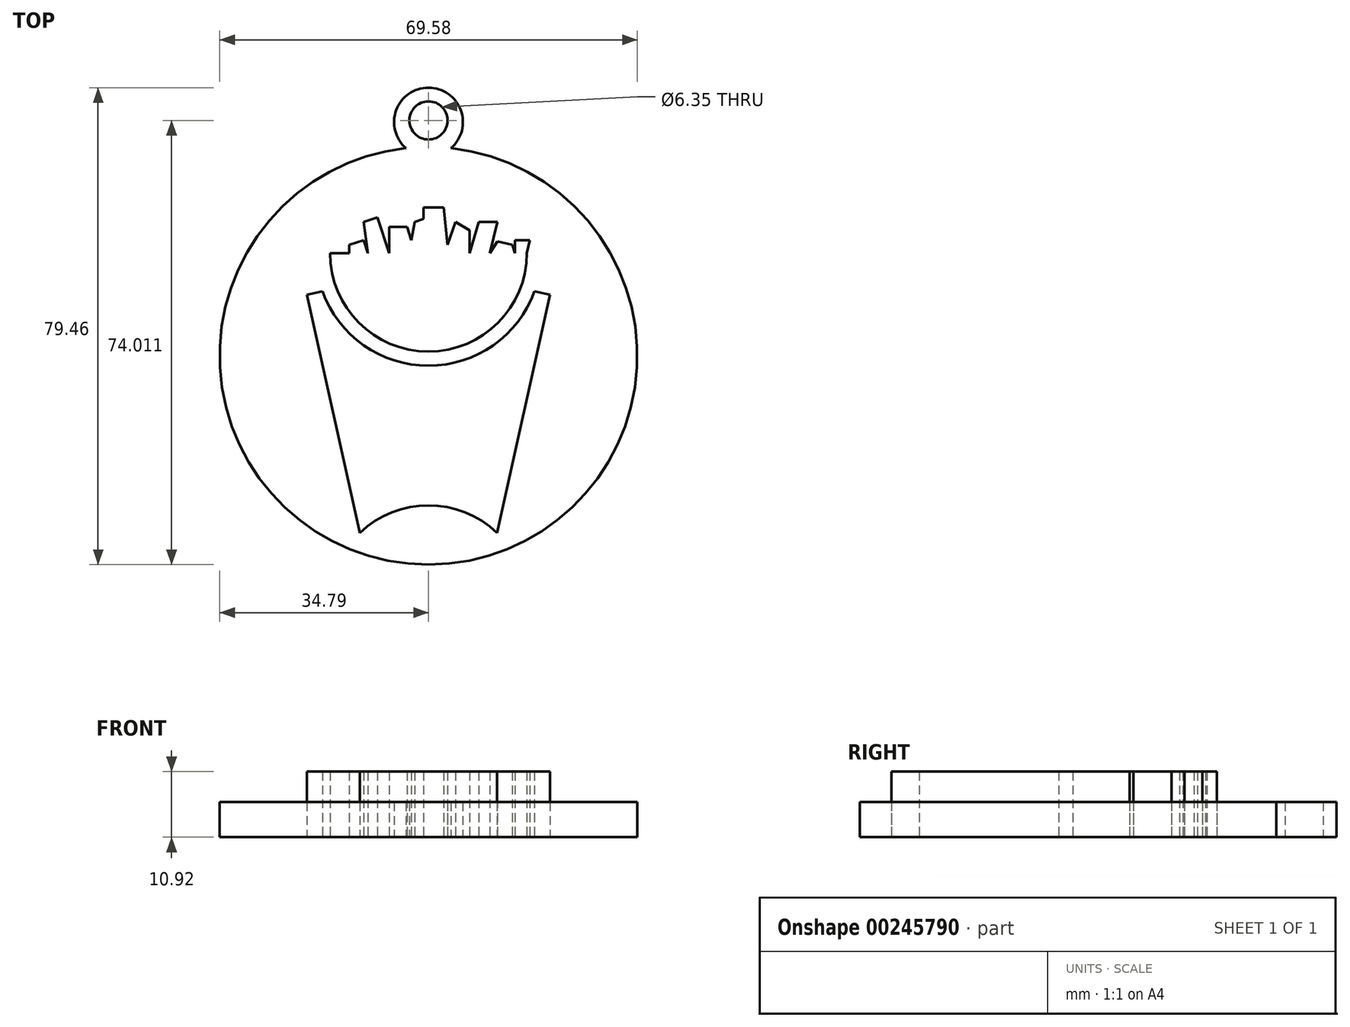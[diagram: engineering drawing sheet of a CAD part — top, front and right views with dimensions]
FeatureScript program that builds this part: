
annotation { "Feature Type Name" : "Feature", "Feature Type Description" : "" }
export const myFeature = defineFeature(function(context is Context, id is Id, definition is map)
    precondition{}
    {
        {
            var Q0;
            Q0=qCreatedBy(makeId("Top.planeOp"),FACE);
            var sketch = newSketch(context, id + "F0", { "sketchPlane" : qUnion([Q0])});
            skCircle(sketch, "E0", {"center": v(0, 0) * mm, "radius": 65.8 * mm});
            skCircle(sketch, "E1", {"center": v(0, 0) * mm, "radius": 57.75 * mm});
            skArc(sketch, "E2", {"start": v(0, 0.7) * mm, "mid": v(11.6, 5.51) * mm, "end": v(16.4, 17.11) * mm});
            skLineSegment(sketch, "E3", {"start": v(11.45, -29.5) * mm, "end": v(20.28, 10.19) * mm});
            skLineSegment(sketch, "E4", {"start": v(20.28, 10.19) * mm, "end": v(17.67, 10.77) * mm});
            skArc(sketch, "E5", {"start": v(0, -1.66) * mm, "mid": v(10.8, 1.76) * mm, "end": v(17.67, 10.77) * mm});
            skArc(sketch, "E6.trimOffspring", {"start": v(11.45, -29.5) * mm, "mid": v(6.17, -26.1) * mm, "end": v(0, -24.92) * mm});
            skLineSegment(sketch, "E7.MirrorCS", {"start": v(-13.24, 17.11) * mm, "end": v(-16.4, 17.11) * mm});
            skArc(sketch, "E8.MirrorCS", {"start": v(0, -1.66) * mm, "mid": v(-10.8, 1.76) * mm, "end": v(-17.67, 10.77) * mm});
            skLineSegment(sketch, "E9.MirrorCS", {"start": v(-11.45, -29.5) * mm, "end": v(-20.28, 10.19) * mm});
            skArc(sketch, "E10.MirrorCS", {"start": v(-11.45, -29.5) * mm, "mid": v(-6.17, -26.1) * mm, "end": v(0, -24.92) * mm});
            skLineSegment(sketch, "E11.MirrorCS", {"start": v(-20.28, 10.19) * mm, "end": v(-17.67, 10.77) * mm});
            skLineSegment(sketch, "E12", {"start": v(-16.4, 17.11) * mm, "end": v(-16.4, 19.07) * mm});
            skLineSegment(sketch, "E13", {"start": v(-16.4, 19.07) * mm, "end": v(-14.15, 19.82) * mm});
            skLineSegment(sketch, "E14", {"start": v(-14.15, 19.82) * mm, "end": v(-13.24, 17.11) * mm});
            skLineSegment(sketch, "E15", {"start": v(-13.24, 17.11) * mm, "end": v(-13.24, 18.47) * mm});
            skPoint(sketch, "E15.endSnap0", {"position": v(-13.7, 18.47) * mm});
            skLineSegment(sketch, "E16", {"start": v(-13.24, 18.47) * mm, "end": v(-10.8, 19.29) * mm});
            skLineSegment(sketch, "E17", {"start": v(-10.8, 19.29) * mm, "end": v(-10.07, 17.11) * mm});
            skLineSegment(sketch, "E18", {"start": v(-10.07, 17.11) * mm, "end": v(-10.8, 22.31) * mm});
            skLineSegment(sketch, "E19", {"start": v(-10.8, 22.31) * mm, "end": v(-8.53, 23.07) * mm});
            skLineSegment(sketch, "E20", {"start": v(-8.53, 23.07) * mm, "end": v(-6.54, 17.11) * mm});
            skLineSegment(sketch, "E21", {"start": v(-6.54, 17.11) * mm, "end": v(-6.54, 21.48) * mm});
            skLineSegment(sketch, "E22", {"start": v(-6.54, 21.48) * mm, "end": v(-3.57, 21.48) * mm});
            skLineSegment(sketch, "E23", {"start": v(-3.57, 21.48) * mm, "end": v(-2.84, 19.29) * mm});
            skLineSegment(sketch, "E24", {"start": v(-2.84, 19.29) * mm, "end": v(-2.29, 22.31) * mm});
            skLineSegment(sketch, "E25", {"start": v(-2.29, 22.31) * mm, "end": v(-0.81, 22.8) * mm});
            skLineSegment(sketch, "E26", {"start": v(-0.81, 22.8) * mm, "end": v(-0.81, 24.73) * mm});
            skLineSegment(sketch, "E27", {"start": v(-0.81, 24.73) * mm, "end": v(2.55, 24.73) * mm});
            skLineSegment(sketch, "E28", {"start": v(2.55, 24.73) * mm, "end": v(3.15, 18.47) * mm});
            skLineSegment(sketch, "E29", {"start": v(3.15, 18.47) * mm, "end": v(4.51, 22.31) * mm});
            skLineSegment(sketch, "E30", {"start": v(4.51, 22.31) * mm, "end": v(6.85, 20.88) * mm});
            skLineSegment(sketch, "E31", {"start": v(6.85, 20.88) * mm, "end": v(6.85, 17.11) * mm});
            skLineSegment(sketch, "E32", {"start": v(6.85, 17.11) * mm, "end": v(8.36, 22.31) * mm});
            skLineSegment(sketch, "E33", {"start": v(8.36, 22.31) * mm, "end": v(11.46, 22.31) * mm});
            skLineSegment(sketch, "E34", {"start": v(11.46, 22.31) * mm, "end": v(10.25, 17.11) * mm});
            skLineSegment(sketch, "E35", {"start": v(10.25, 17.11) * mm, "end": v(11.46, 19.07) * mm});
            skLineSegment(sketch, "E36", {"start": v(11.46, 19.07) * mm, "end": v(13.96, 18.47) * mm});
            skLineSegment(sketch, "E37", {"start": v(13.96, 18.47) * mm, "end": v(14.4, 17.11) * mm});
            skLineSegment(sketch, "E38", {"start": v(14.4, 17.11) * mm, "end": v(14.4, 19.29) * mm});
            skLineSegment(sketch, "E39", {"start": v(14.4, 19.29) * mm, "end": v(16.9, 19.29) * mm});
            skLineSegment(sketch, "E40", {"start": v(16.9, 19.29) * mm, "end": v(16.4, 17.11) * mm});
            skPoint(sketch, "E41.MirrorCS.end.orphan", {"position": v(-16.4, 17.11) * mm});
            skPoint(sketch, "E41.MirrorCS.start.orphan", {"position": v(0, 0.7) * mm});
            skPoint(sketch, "E42.MirrorCS.end.orphan", {"position": v(95.31, 17.11) * mm});
            skPoint(sketch, "E42.MirrorCS.start.orphan", {"position": v(111.72, 0.7) * mm});
            skPoint(sketch, "E43.MirrorCS.end.orphan", {"position": v(-128.13, 17.11) * mm});
            skPoint(sketch, "E43.MirrorCS.start.orphan", {"position": v(-111.72, 0.7) * mm});
            skPoint(sketch, "E44.trimOffspring.end.orphan", {"position": v(16.4, -17.11) * mm});
            skPoint(sketch, "E45.MirrorCS.start.orphan", {"position": v(0, -0.7) * mm});
            skArc(sketch, "E46.MirrorCS", {"start": v(0, 0.7) * mm, "mid": v(-11.6, 5.51) * mm, "end": v(-16.4, 17.11) * mm});
            skSolve(sketch);
        }
        {
            var Q0;
            Q0=makeQuery(id+"F0.imprint","IMPRINT",FACE,{"disambiguationData":[TD([[makeQuery(id+"F0.imprint","IMPRINT",EDGE,{"derivedFrom":sQuery(id+"F0.wireOp",EDGE,"E2")}),1.0]])]});
            var Q1;
            Q1=makeQuery(id+"F0.imprint","IMPRINT",FACE,{"disambiguationData":[TD([[makeQuery(id+"F0.imprint","IMPRINT",EDGE,{"derivedFrom":sQuery(id+"F0.wireOp",EDGE,"E3")}),1.0]])]});
            extrude(context, id + "F1", {"entities" : qUnion([Q0, Q1]), "depth" : 10.92 * mm});
        }
        {
            var Q0;
            Q0=qCreatedBy(makeId("Top.planeOp"),FACE);
            var sketch = newSketch(context, id + "F2", { "sketchPlane" : qUnion([Q0])});
            skCircle(sketch, "E47", {"center": v(0, 0) * mm, "radius": 34.8 * mm});
            skSolve(sketch);
        }
        {
            var Q0;
            Q0=makeQuery(id+"F2.imprint","IMPRINT",FACE,{"disambiguationData":[TD([[makeQuery(id+"F2.imprint","IMPRINT",EDGE,{"derivedFrom":sQuery(id+"F2.wireOp",EDGE,"E47")}),1.0]])]});
            extrude(context, id + "F3", {"entities" : qUnion([Q0]), "depth" : 5.84 * mm});
        }
        {
            var Q0;
            Q0=qCreatedBy(makeId("Top.planeOp"),FACE);
            var sketch = newSketch(context, id + "F4", { "sketchPlane" : qUnion([Q0])});
            skCircle(sketch, "E48", {"center": v(0, 38.94) * mm, "radius": 5.74 * mm});
            skSolve(sketch);
        }
        {
            var Q0;
            Q0=qCreatedBy(makeId("Top.planeOp"),FACE);
            var sketch = newSketch(context, id + "F5", { "sketchPlane" : qUnion([Q0])});
            skSolve(sketch);
        }
        {
            var Q0;
            Q0 = qSketchRegion(id + "F5", true);
            var Q1;
            Q1=makeQuery(id+"F4.imprint","IMPRINT",FACE,{"disambiguationData":[TD([[makeQuery(id+"F4.imprint","IMPRINT",EDGE,{"derivedFrom":sQuery(id+"F4.wireOp",EDGE,"E48")}),1.0]])]});
            extrude(context, id + "F6", {"entities" : qUnion([Q0, Q1]), "operationType" : NewBodyOperationType.ADD, "depth" : 5.84 * mm});
        }
        {
            var Q0;
            Q0=qCreatedBy(makeId("Top.planeOp"),FACE);
            var sketch = newSketch(context, id + "F7", { "sketchPlane" : qUnion([Q0])});
            skCircle(sketch, "E49", {"center": v(0, 39.22) * mm, "radius": 3.06 * mm});
            skSolve(sketch);
        }
        {
            var Q0;
            Q0=sQuery(id+"F7.wireOp",VERTEX,"E49.center");
            var Q1;
            Q1=makeQuery(id+"F3.opExtrude","SWEPT_BODY",BODY,{"disambiguationData":[OSD([sQuery(id+"F2.wireOp",EDGE,"E47")])]});
            hole(context, id + "F8", {"style" : HoleStyle.SIMPLE, "endStyle" : HoleEndStyle.THROUGH, "oppositeDirection" : true, "holeDiameter" : 6.35 * mm, "tappedDepth" : 12.7 * mm, "tapClearance" : 3, "locations" : qUnion([Q0]), "scope" : qUnion([Q1])});
        }
    });
